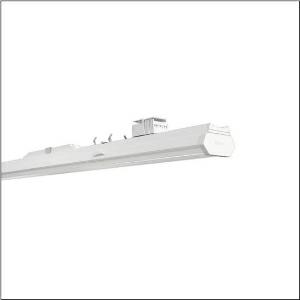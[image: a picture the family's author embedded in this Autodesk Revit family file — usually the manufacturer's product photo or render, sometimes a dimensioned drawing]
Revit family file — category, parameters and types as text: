
# Revit family: licross_11_protected_mo_51td12mn4axg
name_source: partatom
category: Lighting Fixtures
units: mm (PartAtom-declared; Revit-internal decimal feet)

## family parameters
Cut with Voids When Loaded = No
Host = Face
Light Source = No
Part Type = Normal
Room Calculation Point = No
Round Connector Dimension = Use Diameter
Shared = No

## types (1)
- --- (1 x LED, 10020 lm, 55.3 W, 4000K)
    Apparent Load = 55 VA
    CIE Flux Codes = 73 92 98 99 100
    Color Rendering = 80
    Color Temperature = 4000K
    Default Elevation = 1800 mm
    Description = Licross 11 Protected MO, luminaire insert, of sheet steel, galvanised, coil coated, white, length: 1.500mm, width: 90mm, height: 101mm, LED rated luminous flux: 10.030lm, light colour: 840, SDCM (Standard Deviation of Colour Matching)MacAdam ≤ 2 SDCM (initial), control gear: ON/OFF Multilumen, with plug, 3-pole, with phase selection, mains connection: 220..240V, AC, 50/60Hz, rated input power: 55W, internal wiring halogen-free, primary light control with lens, of plastic, primary optical cover: cover, of PMMA, light emission: direct distribution, primary light characteristic: symmetric, protection rating (complete): IP54, insulation class (complete): insulation class I (protective earthing), certification: CE, ENEC, VDE, UKCA, protection symbol: D if used in an environment with non-conductive dust loads with corresponding accessories, impact resistance: IK06, permissible ambient temperature for indoor applications: -35..+40°C, corresponds to IFS (International Featured Standards) requirements for safety and quality in the food industry, reducing of maximum allowable ambient temperature of 5°C with ceiling mounting, LABS conformity tested according to VDMA 24364:2018-05, The light source and the operating device comply with the requirements of the Ecodesign Regulation (EU) 2019/2020 and are replaceable in accordance with this regulation, packaging unit: 1 piece
    Height = 92 mm
    Lamp = 1 x LED
    Lamp Light Flux = 10020 lm
    Lamp Power = 55.3 W
    Lamp count = 1
    Length = 1500 mm
    Luminous efficacy = 181 lm/W
    Manufacturer = Siteco
    ModVariant = No
    Model = 51TD12MN4AXG
    Mounting Place = Ceiling
    Mounting Type = Pendant
    Number of Poles = 1
    OnlyDefault = Yes
    Power Factor = 1
    Product Name = Licross 11 Protected MO
    Product group = luminaire insert | ceiling pendant
    ProductGroupID = 901
    Protection Class = Protection class I
    Protection Degree = IP 54
    RLX_Detail_Level = 1
    RLX_Emergency_Light_Flux = 0 lm
    RLX_Emergency_Type = 0
    RLX_Emergency_Type_DB = No
    RlxData = <blob elided: 22349 chars, md5=9f02f294>
    Socket = socket
    Standby Power = 0 W
    System Light Flux = 10020 lm
    System Power = 55 W
    Type Comments = factory setting: luminous flux: 100 % | (A | C | E) | 126 mA
    Type Image = l_1256145.jpg
    URL = http://relux.com
    VarID = @adj_090473
    Voltage = 0 V
    Weight = 0.00 kg
    Width = 88 mm

## geometry (parser evidence)
native form markers: Blend x4, Sweep x11
no freeform markers — native parametric forms only
